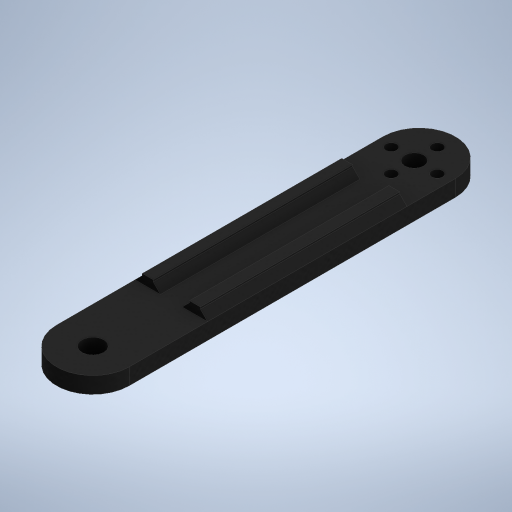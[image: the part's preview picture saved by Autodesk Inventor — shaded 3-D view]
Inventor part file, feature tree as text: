
AUTODESK INVENTOR PART (.ipt)
format: ipt  version: 2023 (Build 270158000, 158)  size: 484,352 bytes
history: native  units: mm
features: extrude x5, sketch x4, other x1, fillet x1, chamfer x1
ambient origin geometry x8: Origin, YZ Plane, XZ Plane, XY Plane, X Axis, Y Axis, Z Axis, Center Point
bodies: Body1 (feature_tree)
feature tree (12):
  other  "Bryła1"
  sketch  "Szkic1"
  extrude  "Wyciągnięcie proste1"  Depth=20.0mm
  sketch  "Szkic3"
  fillet  "Zaokrąglenie1"  Radius=110.0mm
  extrude  "Wyciągnięcie proste4"  Depth=5.2mm
  extrude  "Wyciągnięcie proste5"  Depth=3.0mm
  extrude  "Wyciągnięcie proste6"  Depth=3.0mm
  extrude  "Wyciągnięcie proste7"  Depth=6.35mm
  chamfer  "Faza1"  Distance=6.35mm
  sketch  "Szkic4"
  sketch  "Szkic5"
